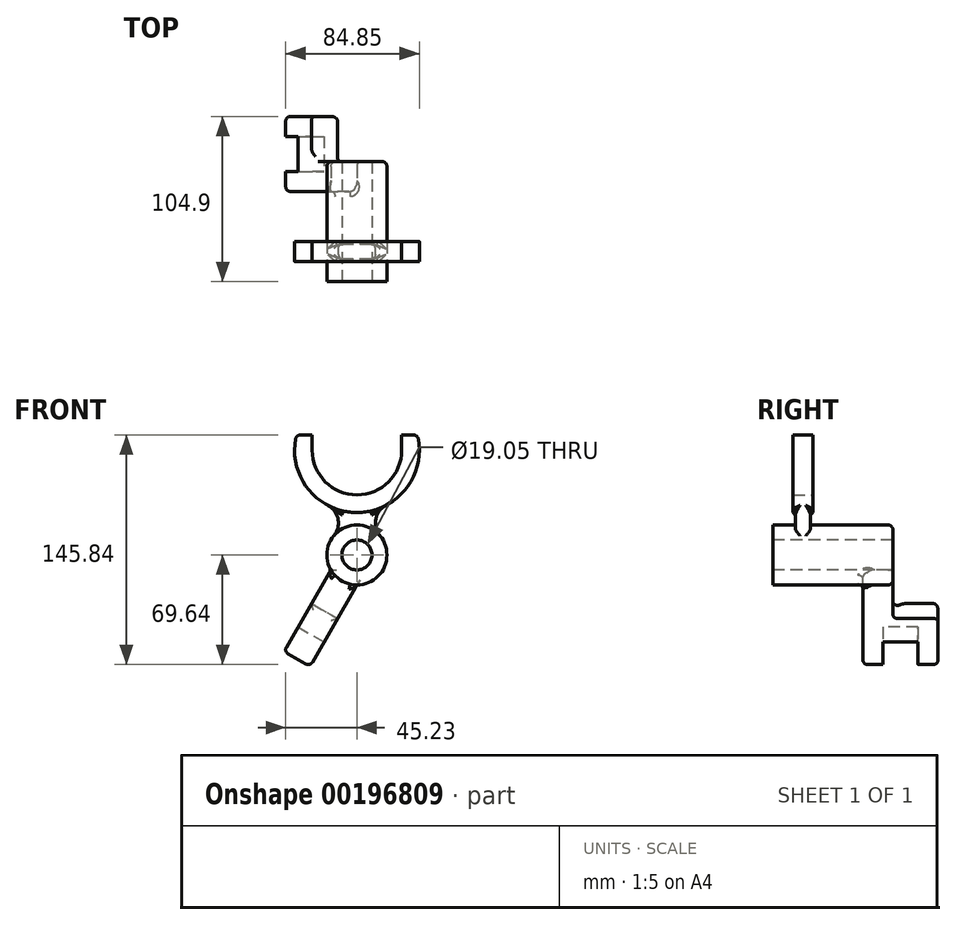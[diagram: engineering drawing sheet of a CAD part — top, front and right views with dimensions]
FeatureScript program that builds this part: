
annotation { "Feature Type Name" : "Feature", "Feature Type Description" : "" }
export const myFeature = defineFeature(function(context is Context, id is Id, definition is map)
    precondition{}
    {
        {
            var Q0;
            Q0=qCreatedBy(makeId("Front.planeOp"),FACE);
            var sketch = newSketch(context, id + "F0", { "sketchPlane" : qUnion([Q0])});
            skCircle(sketch, "E0", {"center": v(0, 0) * mm, "radius": 19.05 * mm});
            skSolve(sketch);
        }
        {
            var Q0;
            Q0=makeQuery(id+"F0.imprint","IMPRINT",FACE,{"disambiguationData":[TD([[makeQuery(id+"F0.imprint","IMPRINT",EDGE,{"derivedFrom":sQuery(id+"F0.wireOp",EDGE,"E0")}),1.0]])]});
            extrude(context, id + "F1", {"entities" : qUnion([Q0]), "oppositeDirection" : true, "depth" : 76.2 * mm});
        }
        {
            var Q0;
            Q0=makeQuery(id+"F1.opExtrude","CAP_FACE",FACE,{"disambiguationData":[OSD([sQuery(id+"F0.wireOp",EDGE,"E0"),sQuery(id+"F0.wireOp",EDGE,"9t7G7Edk-k1pP-L33E-AeWF-xE0Gkoiz6W2Z")])],"isStart":true});
            cPlane(context, id + "F2", {"entities" : qUnion([Q0]), "cplaneType" : CPlaneType.OFFSET, "offset" : 19.05 * mm, "oppositeDirection" : true, "width" : 152.4 * mm, "height" : 152.4 * mm});
        }
        {
            var Q0;
            Q0=qCreatedBy(id+"F2.planeOp",FACE);
            var sketch = newSketch(context, id + "F3", { "sketchPlane" : qUnion([Q0])});
            skArc(sketch, "E1", {"start": v(-28.45, 66.55) * mm, "mid": v(0, 38.1) * mm, "end": v(28.45, 66.55) * mm});
            skLineSegment(sketch, "E2", {"start": v(-28.45, 66.55) * mm, "end": v(-28.45, 76.2) * mm});
            skLineSegment(sketch, "E3", {"start": v(28.45, 66.55) * mm, "end": v(28.45, 76.2) * mm});
            skLineSegment(sketch, "E4", {"start": v(28.45, 76.2) * mm, "end": v(35.97, 76.2) * mm});
            skLineSegment(sketch, "E5", {"start": v(-28.45, 76.2) * mm, "end": v(-35.97, 76.2) * mm});
            skArc(sketch, "E6.trimOffspring", {"start": v(-38.97, 73.7) * mm, "mid": v(-35.65, 49.25) * mm, "end": v(-18.5, 31.5) * mm});
            skPoint(sketch, "E7.visualSharp", {"position": v(-38.43, 76.2) * mm});
            skArc(sketch, "E7.filletArc", {"start": v(-35.97, 76.2) * mm, "mid": v(-37.93, 75.5) * mm, "end": v(-38.97, 73.7) * mm});
            skPoint(sketch, "E8.visualSharp", {"position": v(38.43, 76.2) * mm});
            skArc(sketch, "E8.filletArc", {"start": v(38.97, 73.7) * mm, "mid": v(37.93, 75.5) * mm, "end": v(35.97, 76.2) * mm});
            skArc(sketch, "E9", {"start": v(14.66, 12.17) * mm, "mid": v(0, 19.05) * mm, "end": v(-14.66, 12.17) * mm});
            skArc(sketch, "E10", {"start": v(18.5, 31.5) * mm, "mid": v(11.97, 22.75) * mm, "end": v(14.66, 12.17) * mm});
            skArc(sketch, "E11", {"start": v(-14.66, 12.17) * mm, "mid": v(-11.97, 22.75) * mm, "end": v(-18.5, 31.5) * mm});
            skArc(sketch, "E12.trimOffspring", {"start": v(18.5, 31.5) * mm, "mid": v(35.65, 49.25) * mm, "end": v(38.97, 73.7) * mm});
            skSolve(sketch);
        }
        {
            var Q0;
            Q0=qCreatedBy(id+"F2.planeOp",FACE);
            var sketch = newSketch(context, id + "F4", { "sketchPlane" : qUnion([Q0])});
            skArc(sketch, "E13", {"start": v(-28.45, 66.55) * mm, "mid": v(0, 38.1) * mm, "end": v(28.45, 66.55) * mm});
            skArc(sketch, "E14", {"start": v(-38.97, 73.7) * mm, "mid": v(0, 26.92) * mm, "end": v(38.97, 73.7) * mm});
            skLineSegment(sketch, "E15", {"start": v(28.45, 76.2) * mm, "end": v(35.97, 76.2) * mm});
            skLineSegment(sketch, "E16", {"start": v(-28.45, 76.2) * mm, "end": v(-35.97, 76.2) * mm});
            skPoint(sketch, "E17.visualSharp", {"position": v(-38.43, 76.2) * mm});
            skArc(sketch, "E17.filletArc", {"start": v(-35.97, 76.2) * mm, "mid": v(-37.93, 75.5) * mm, "end": v(-38.97, 73.7) * mm});
            skPoint(sketch, "E18.visualSharp", {"position": v(38.43, 76.2) * mm});
            skArc(sketch, "E18.filletArc", {"start": v(38.97, 73.7) * mm, "mid": v(37.93, 75.5) * mm, "end": v(35.97, 76.2) * mm});
            skLineSegment(sketch, "E19", {"start": v(-28.45, 66.55) * mm, "end": v(-28.45, 76.2) * mm});
            skLineSegment(sketch, "E20", {"start": v(28.45, 66.55) * mm, "end": v(28.45, 76.2) * mm});
            skSolve(sketch);
        }
        {
            var Q0;
            Q0 = qSketchRegion(id + "F3", true);
            extrude(context, id + "F5", {"entities" : qUnion([Q0]), "operationType" : NewBodyOperationType.ADD, "endBound" : BoundingType.SYMMETRIC, "depth" : 9.65 * mm});
        }
        {
            var Q0;
            Q0 = qSketchRegion(id + "F4", true);
            extrude(context, id + "F6", {"entities" : qUnion([Q0]), "operationType" : NewBodyOperationType.ADD, "endBound" : BoundingType.SYMMETRIC, "depth" : 12.7 * mm});
        }
        {
            var Q0;
            Q0=makeQuery(id+"F5.opExtrude","CAP_EDGE",EDGE,{"disambiguationData":[OSD([sQuery(id+"F3.wireOp",EDGE,"E11")])],"isStart":false});
            var Q1;
            Q1=makeQuery(id+"F5.opExtrude","CAP_EDGE",EDGE,{"disambiguationData":[OSD([sQuery(id+"F3.wireOp",EDGE,"E10")])],"isStart":false});
            fillet(context, id + "F7", {"entities" : qUnion([Q0, Q1]), "radius" : 3.05 * mm, "tangentPropagation" : true, "allowEdgeOverflow" : false});
        }
        {
            var Q0;
            Q0=makeQuery(id+"F5.opExtrude","CAP_EDGE",EDGE,{"disambiguationData":[OSD([sQuery(id+"F3.wireOp",EDGE,"E10")])],"isStart":true});
            var Q1;
            Q1=makeQuery(id+"F5.opExtrude","CAP_EDGE",EDGE,{"disambiguationData":[OSD([sQuery(id+"F3.wireOp",EDGE,"E11")])],"isStart":true});
            fillet(context, id + "F8", {"entities" : qUnion([Q0, Q1]), "radius" : 3.05 * mm, "tangentPropagation" : true, "allowEdgeOverflow" : false});
        }
        {
            var Q0;
            Q0=makeQuery(id+"F5.opExtrude","CAP_EDGE",EDGE,{"disambiguationData":[OSD([sQuery(id+"F3.wireOp",EDGE,"E9")])],"isStart":false});
            var Q1;
            Q1=makeQuery(id+"F5.opExtrude","CAP_EDGE",EDGE,{"disambiguationData":[OSD([sQuery(id+"F3.wireOp",EDGE,"E9")])],"isStart":true});
            var Q2;
            Q2=makeQuery(id+"F6.boolean.opBoolean","INTERSECT",EDGE,{"derivedFrom":[makeQuery(id+"F5.opExtrude","CAP_FACE",FACE,{"disambiguationData":[OSD([sQuery(id+"F3.wireOp",EDGE,"E1"),sQuery(id+"F3.wireOp",EDGE,"E2"),sQuery(id+"F3.wireOp",EDGE,"E3"),sQuery(id+"F3.wireOp",EDGE,"E4"),sQuery(id+"F3.wireOp",EDGE,"E5"),sQuery(id+"F3.wireOp",EDGE,"E6.trimOffspring"),sQuery(id+"F3.wireOp",EDGE,"E7.filletArc"),sQuery(id+"F3.wireOp",EDGE,"E8.filletArc"),sQuery(id+"F3.wireOp",EDGE,"E9"),sQuery(id+"F3.wireOp",EDGE,"E10"),sQuery(id+"F3.wireOp",EDGE,"E11"),sQuery(id+"F3.wireOp",EDGE,"E12.trimOffspring")])],"isStart":false}),makeQuery(id+"F6.opExtrude","SWEPT_FACE",FACE,{"disambiguationData":[OSD([sQuery(id+"F4.wireOp",EDGE,"E14")])]})]});
            var Q3;
            Q3=makeQuery(id+"F6.boolean.opBoolean","INTERSECT",EDGE,{"derivedFrom":[makeQuery(id+"F5.opExtrude","CAP_FACE",FACE,{"disambiguationData":[OSD([sQuery(id+"F3.wireOp",EDGE,"E1"),sQuery(id+"F3.wireOp",EDGE,"E2"),sQuery(id+"F3.wireOp",EDGE,"E3"),sQuery(id+"F3.wireOp",EDGE,"E4"),sQuery(id+"F3.wireOp",EDGE,"E5"),sQuery(id+"F3.wireOp",EDGE,"E6.trimOffspring"),sQuery(id+"F3.wireOp",EDGE,"E7.filletArc"),sQuery(id+"F3.wireOp",EDGE,"E8.filletArc"),sQuery(id+"F3.wireOp",EDGE,"E9"),sQuery(id+"F3.wireOp",EDGE,"E10"),sQuery(id+"F3.wireOp",EDGE,"E11"),sQuery(id+"F3.wireOp",EDGE,"E12.trimOffspring")])],"isStart":true}),makeQuery(id+"F6.opExtrude","SWEPT_FACE",FACE,{"disambiguationData":[OSD([sQuery(id+"F4.wireOp",EDGE,"E14")])]})]});
            fillet(context, id + "F9", {"entities" : qUnion([Q0, Q1, Q2, Q3]), "radius" : 3.05 * mm, "tangentPropagation" : true, "allowEdgeOverflow" : false});
        }
        {
            var Q0;
            Q0=makeQuery(id+"F1.opExtrude","SWEPT_FACE",FACE,{"disambiguationData":[OSD([sQuery(id+"F0.wireOp",EDGE,"9t7G7Edk-k1pP-L33E-AeWF-xE0Gkoiz6W2Z")])]});
            var Q1;
            Q1=qCreatedBy(makeId("Right.planeOp"),FACE);
            var Q2;
            Q2=makeQuery(id+"F1.opExtrude","SWEPT_FACE",FACE,{"disambiguationData":[OSD([sQuery(id+"F0.wireOp",EDGE,"E0")])]});
            cPlane(context, id + "F10", {"entities" : qUnion([Q0, Q1, Q2]), "cplaneType" : CPlaneType.LINE_ANGLE, "offset" : 25.4 * mm, "angle" : 330 * degree, "width" : 152.4 * mm, "height" : 152.4 * mm});
        }
        {
            var Q0;
            Q0=qCreatedBy(id+"F10.planeOp",FACE);
            var sketch = newSketch(context, id + "F11", { "sketchPlane" : qUnion([Q0])});
            skLineSegment(sketch, "E21", {"start": v(-57.15, 0) * mm, "end": v(-76.2, 0) * mm});
            skLineSegment(sketch, "E22", {"start": v(-76.2, 0) * mm, "end": v(-76.2, -41.15) * mm});
            skLineSegment(sketch, "E23", {"start": v(-76.2, -41.15) * mm, "end": v(-104.9, -41.15) * mm});
            skLineSegment(sketch, "E24", {"start": v(-104.9, -41.15) * mm, "end": v(-104.9, -76.2) * mm});
            skLineSegment(sketch, "E25", {"start": v(-104.9, -76.2) * mm, "end": v(-92.2, -76.2) * mm});
            skLineSegment(sketch, "E26", {"start": v(-92.2, -76.2) * mm, "end": v(-92.2, -58.42) * mm});
            skLineSegment(sketch, "E27", {"start": v(-92.2, -58.42) * mm, "end": v(-69.85, -58.42) * mm});
            skLineSegment(sketch, "E28", {"start": v(-69.85, -58.42) * mm, "end": v(-69.85, -76.2) * mm});
            skLineSegment(sketch, "E29", {"start": v(-69.85, -76.2) * mm, "end": v(-57.15, -76.2) * mm});
            skLineSegment(sketch, "E30", {"start": v(-57.15, -76.2) * mm, "end": v(-57.15, 0) * mm});
            skLineSegment(sketch, "E31", {"start": v(-76.2, 0) * mm, "end": v(-57.15, 0) * mm});
            skSolve(sketch);
        }
        {
            var Q0;
            Q0=makeQuery(id+"F11.imprint","IMPRINT",FACE,{"disambiguationData":[TD([[makeQuery(id+"F11.imprint","IMPRINT",EDGE,{"derivedFrom":sQuery(id+"F11.wireOp",EDGE,"E22")}),1.0]])]});
            extrude(context, id + "F12", {"entities" : qUnion([Q0]), "operationType" : NewBodyOperationType.ADD, "endBound" : BoundingType.SYMMETRIC, "depth" : 19.05 * mm});
        }
        {
            var Q0;
            Q0=makeQuery(id+"F12.opExtrude","CAP_EDGE",EDGE,{"disambiguationData":[OSD([sQuery(id+"F11.wireOp",EDGE,"E29")])],"isStart":true});
            var Q1;
            Q1=makeQuery(id+"F12.opExtrude","SWEPT_EDGE",EDGE,{"disambiguationData":[OSD([sQuery(id+"F11.wireOp",EDGE,"E29"),sQuery(id+"F11.wireOp",EDGE,"E30")])]});
            var Q2;
            Q2=makeQuery(id+"F12.opExtrude","CAP_EDGE",EDGE,{"disambiguationData":[OSD([sQuery(id+"F11.wireOp",EDGE,"E29")])],"isStart":false});
            var Q3;
            Q3=makeQuery(id+"F12.opExtrude","CAP_EDGE",EDGE,{"disambiguationData":[OSD([sQuery(id+"F11.wireOp",EDGE,"E30")])],"isStart":true});
            var Q4;
            Q4=makeQuery(id+"F12.boolean.opBoolean","INTERSECT",EDGE,{"derivedFrom":[makeQuery(id+"F1.opExtrude","SWEPT_FACE",FACE,{"disambiguationData":[OSD([sQuery(id+"F0.wireOp",EDGE,"E0")])]}),makeQuery(id+"F12.opExtrude","SWEPT_FACE",FACE,{"disambiguationData":[OSD([sQuery(id+"F11.wireOp",EDGE,"E30")])]})]});
            var Q5;
            Q5=makeQuery(id+"F12.opExtrude","SWEPT_EDGE",EDGE,{"disambiguationData":[OSD([sQuery(id+"F11.wireOp",EDGE,"E22"),sQuery(id+"F11.wireOp",EDGE,"E23")])]});
            var Q6;
            Q6=makeQuery(id+"F12.opExtrude","CAP_EDGE",EDGE,{"disambiguationData":[OSD([sQuery(id+"F11.wireOp",EDGE,"E22")])],"isStart":false});
            var Q7;
            Q7=makeQuery(id+"F1.opExtrude","CAP_EDGE",EDGE,{"disambiguationData":[OSD([sQuery(id+"F0.wireOp",EDGE,"E0")])],"isStart":false});
            var Q8;
            Q8=makeQuery(id+"F12.opExtrude","CAP_EDGE",EDGE,{"disambiguationData":[OSD([sQuery(id+"F11.wireOp",EDGE,"E24")])],"isStart":true});
            var Q9;
            Q9=makeQuery(id+"F12.opExtrude","SWEPT_EDGE",EDGE,{"disambiguationData":[OSD([sQuery(id+"F11.wireOp",EDGE,"E23"),sQuery(id+"F11.wireOp",EDGE,"E24")])]});
            var Q10;
            Q10=makeQuery(id+"F12.opExtrude","CAP_EDGE",EDGE,{"disambiguationData":[OSD([sQuery(id+"F11.wireOp",EDGE,"E24")])],"isStart":false});
            var Q11;
            Q11=makeQuery(id+"F12.opExtrude","CAP_EDGE",EDGE,{"disambiguationData":[OSD([sQuery(id+"F11.wireOp",EDGE,"E30")])],"isStart":false});
            var Q12;
            Q12=makeQuery(id+"F12.opExtrude","CAP_EDGE",EDGE,{"disambiguationData":[OSD([sQuery(id+"F11.wireOp",EDGE,"E25")])],"isStart":false});
            var Q13;
            Q13=makeQuery(id+"F12.opExtrude","CAP_EDGE",EDGE,{"disambiguationData":[OSD([sQuery(id+"F11.wireOp",EDGE,"E25")])],"isStart":true});
            var Q14;
            Q14=makeQuery(id+"F12.opExtrude","SWEPT_EDGE",EDGE,{"disambiguationData":[OSD([sQuery(id+"F11.wireOp",EDGE,"E24"),sQuery(id+"F11.wireOp",EDGE,"E25")])]});
            fillet(context, id + "F13", {"entities" : qUnion([Q0, Q1, Q2, Q3, Q4, Q5, Q6, Q7, Q8, Q9, Q10, Q11, Q12, Q13, Q14]), "radius" : 3.05 * mm, "tangentPropagation" : true, "allowEdgeOverflow" : false});
        }
        {
            var Q0;
            Q0=makeQuery(id+"F1.opExtrude","CAP_FACE",FACE,{"disambiguationData":[OSD([sQuery(id+"F0.wireOp",EDGE,"E0")])],"isStart":true});
            var sketch = newSketch(context, id + "F14", { "sketchPlane" : qUnion([Q0])});
            skCircle(sketch, "E32", {"center": v(0, 0) * mm, "radius": 9.53 * mm});
            skSolve(sketch);
        }
        {
            var Q0;
            Q0=makeQuery(id+"F14.imprint","IMPRINT",FACE,{"disambiguationData":[TD([[makeQuery(id+"F14.imprint","IMPRINT",EDGE,{"derivedFrom":sQuery(id+"F14.wireOp",EDGE,"E32")}),1.0]])]});
            extrude(context, id + "F15", {"entities" : qUnion([Q0]), "operationType" : NewBodyOperationType.REMOVE, "endBound" : BoundingType.THROUGH_ALL, "oppositeDirection" : true, "depth" : 25.4 * mm});
        }
    });
